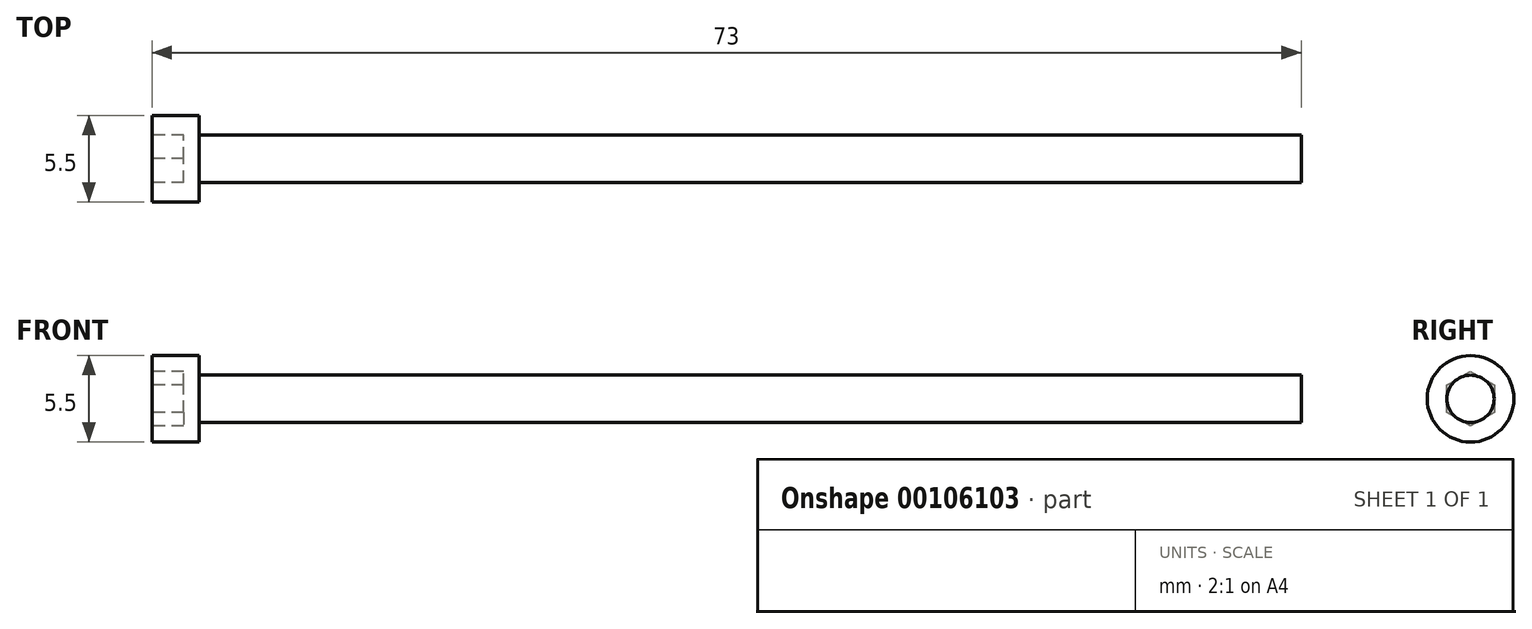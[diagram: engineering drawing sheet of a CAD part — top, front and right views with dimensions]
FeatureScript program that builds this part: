
annotation { "Feature Type Name" : "Feature", "Feature Type Description" : "" }
export const myFeature = defineFeature(function(context is Context, id is Id, definition is map)
    precondition{}
    {
        {
            var Q0;
            Q0=qCreatedBy(makeId("Right.planeOp"),FACE);
            var sketch = newSketch(context, id + "F0", { "sketchPlane" : qUnion([Q0])});
            skCircle(sketch, "E0.cCircle", {"center": v(0, 0) * mm, "radius": 1.5 * mm, "construction": true});
            skLineSegment(sketch, "E0.0", {"start": v(-1.5, 0.87) * mm, "end": v(0, 1.73) * mm});
            skLineSegment(sketch, "E0.1", {"start": v(0, 1.73) * mm, "end": v(1.5, 0.87) * mm});
            skLineSegment(sketch, "E0.2", {"start": v(1.5, 0.87) * mm, "end": v(1.5, -0.87) * mm});
            skLineSegment(sketch, "E0.3", {"start": v(1.5, -0.87) * mm, "end": v(0, -1.73) * mm});
            skLineSegment(sketch, "E0.4", {"start": v(0, -1.73) * mm, "end": v(-1.5, -0.87) * mm});
            skLineSegment(sketch, "E0.5", {"start": v(-1.5, -0.87) * mm, "end": v(-1.5, 0.87) * mm});
            skPoint(sketch, "E0.0.midPoint", {"position": v(-0.75, 1.3) * mm});
            skCircle(sketch, "E1", {"center": v(0, 0) * mm, "radius": 2.75 * mm});
            skSolve(sketch);
        }
        {
            var Q0;
            Q0=makeQuery(id+"F0.imprint","IMPRINT",FACE,{"disambiguationData":[TD([[makeQuery(id+"F0.imprint","IMPRINT",EDGE,{"derivedFrom":sQuery(id+"F0.wireOp",EDGE,"E0.0")}),1.0]])]});
            extrude(context, id + "F1", {"entities" : qUnion([Q0]), "depth" : 2 * mm});
        }
        {
            var Q0;
            Q0=makeQuery(id+"F1.opExtrude","CAP_FACE",FACE,{"disambiguationData":[OSD([sQuery(id+"F0.wireOp",EDGE,"E0.0"),sQuery(id+"F0.wireOp",EDGE,"E0.1"),sQuery(id+"F0.wireOp",EDGE,"E0.2"),sQuery(id+"F0.wireOp",EDGE,"E0.3"),sQuery(id+"F0.wireOp",EDGE,"E0.4"),sQuery(id+"F0.wireOp",EDGE,"E0.5"),sQuery(id+"F0.wireOp",EDGE,"E1")])],"isStart":false});
            var sketch = newSketch(context, id + "F2", { "sketchPlane" : qUnion([Q0])});
            skCircle(sketch, "E2", {"center": v(0, 0) * mm, "radius": 2.75 * mm});
            skSolve(sketch);
        }
        {
            var Q0;
            Q0=qSketchRegion(id+"F2",true);
            extrude(context, id + "F3", {"entities" : qUnion([Q0]), "operationType" : NewBodyOperationType.ADD, "depth" : 1 * mm});
        }
        {
            var Q0;
            Q0=makeQuery(id+"F3.opExtrude","CAP_FACE",FACE,{"disambiguationData":[OSD([sQuery(id+"F2.wireOp",EDGE,"E2")])],"isStart":false});
            var sketch = newSketch(context, id + "F4", { "sketchPlane" : qUnion([Q0])});
            skCircle(sketch, "E3", {"center": v(0, 0) * mm, "radius": 1.5 * mm});
            skSolve(sketch);
        }
        {
            var Q0;
            Q0=qSketchRegion(id+"F4",true);
            extrude(context, id + "F5", {"entities" : qUnion([Q0]), "operationType" : NewBodyOperationType.ADD, "depth" : 70 * mm});
        }
    });
